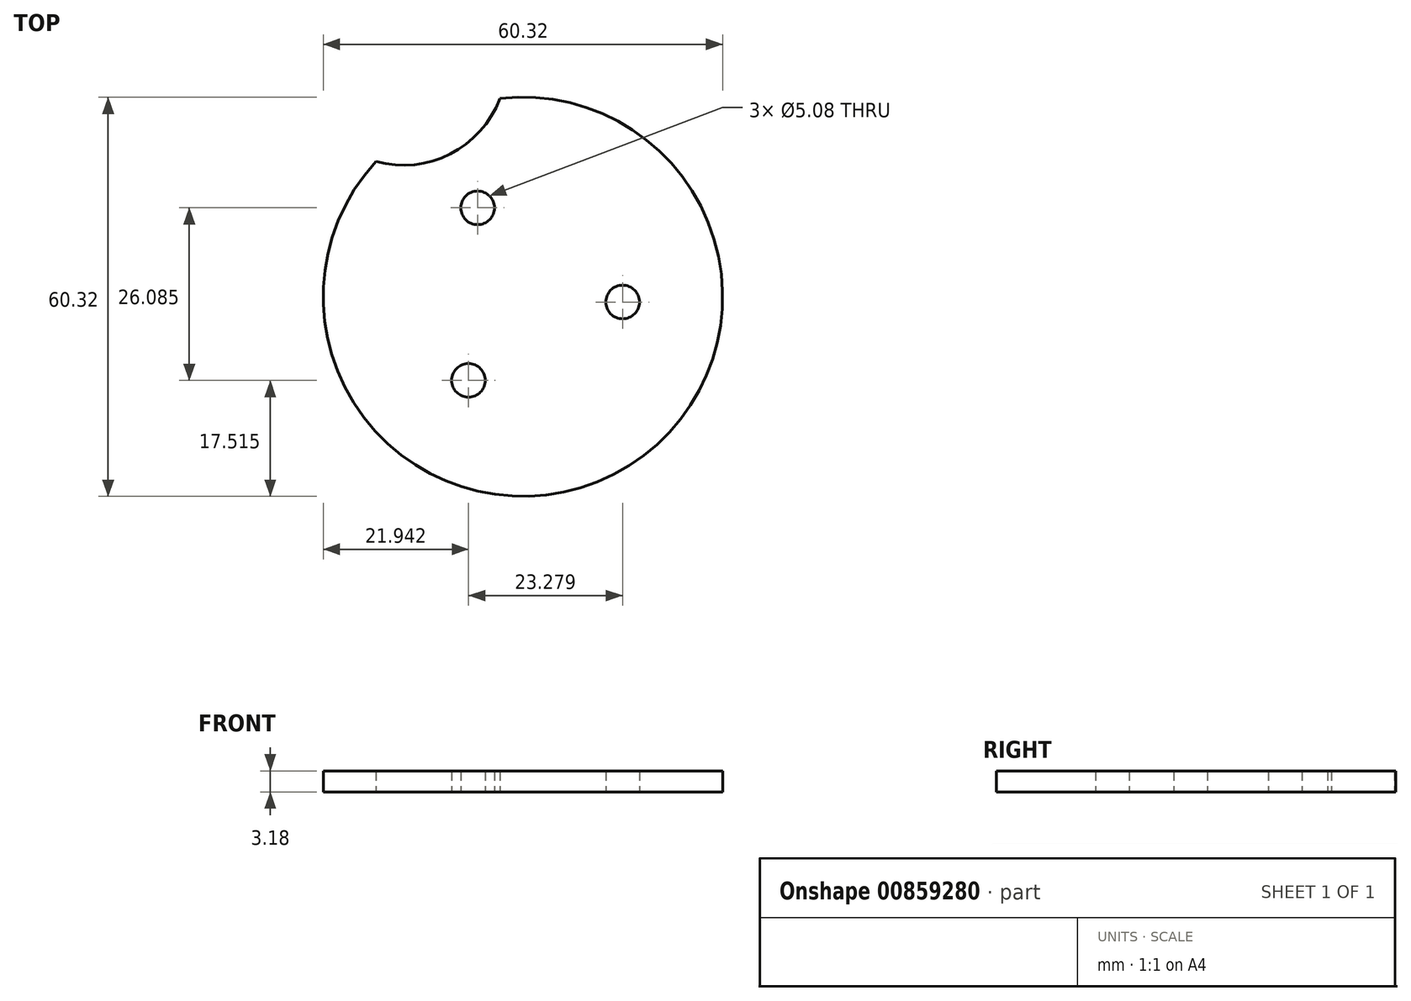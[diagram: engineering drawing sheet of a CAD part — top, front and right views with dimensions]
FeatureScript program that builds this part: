
annotation { "Feature Type Name" : "Feature", "Feature Type Description" : "" }
export const myFeature = defineFeature(function(context is Context, id is Id, definition is map)
    precondition{}
    {
        {
            var Q0;
            Q0=qCreatedBy(makeId("Top.planeOp"),FACE);
            var sketch = newSketch(context, id + "F0", { "sketchPlane" : qUnion([Q0])});
            skArc(sketch, "E0", {"start": v(-22.19, 20.43) * mm, "mid": v(13.68, -26.88) * mm, "end": v(-3.47, 29.96) * mm});
            skArc(sketch, "E1.cCircle", {"start": v(-22.19, 20.43) * mm, "mid": v(13.68, -26.88) * mm, "end": v(-3.47, 29.96) * mm, "construction": true});
            skPoint(sketch, "E2", {"position": v(15.06, -0.8) * mm});
            skPoint(sketch, "E3", {"position": v(-8.22, -12.65) * mm});
            skPoint(sketch, "E4", {"position": v(-6.84, 13.44) * mm});
            skCircle(sketch, "E5", {"center": v(-8.22, -12.65) * mm, "radius": 2.54 * mm});
            skCircle(sketch, "E6", {"center": v(-6.84, 13.44) * mm, "radius": 2.54 * mm});
            skCircle(sketch, "E7", {"center": v(15.06, -0.8) * mm, "radius": 2.54 * mm});
            skArc(sketch, "E8", {"start": v(-22.19, 20.43) * mm, "mid": v(-10.98, 21.57) * mm, "end": v(-3.47, 29.96) * mm});
            skCircle(sketch, "E9.cCircle", {"center": v(0, 0) * mm, "radius": 30.16 * mm, "construction": true});
            skSolve(sketch);
        }
        {
            var Q0;
            Q0 = qSketchRegion(id + "F0", true);
            extrude(context, id + "F1", {"entities" : qUnion([Q0]), "depth" : 3.17 * mm, "offsetDistance" : 25.4 * mm});
        }
    });
